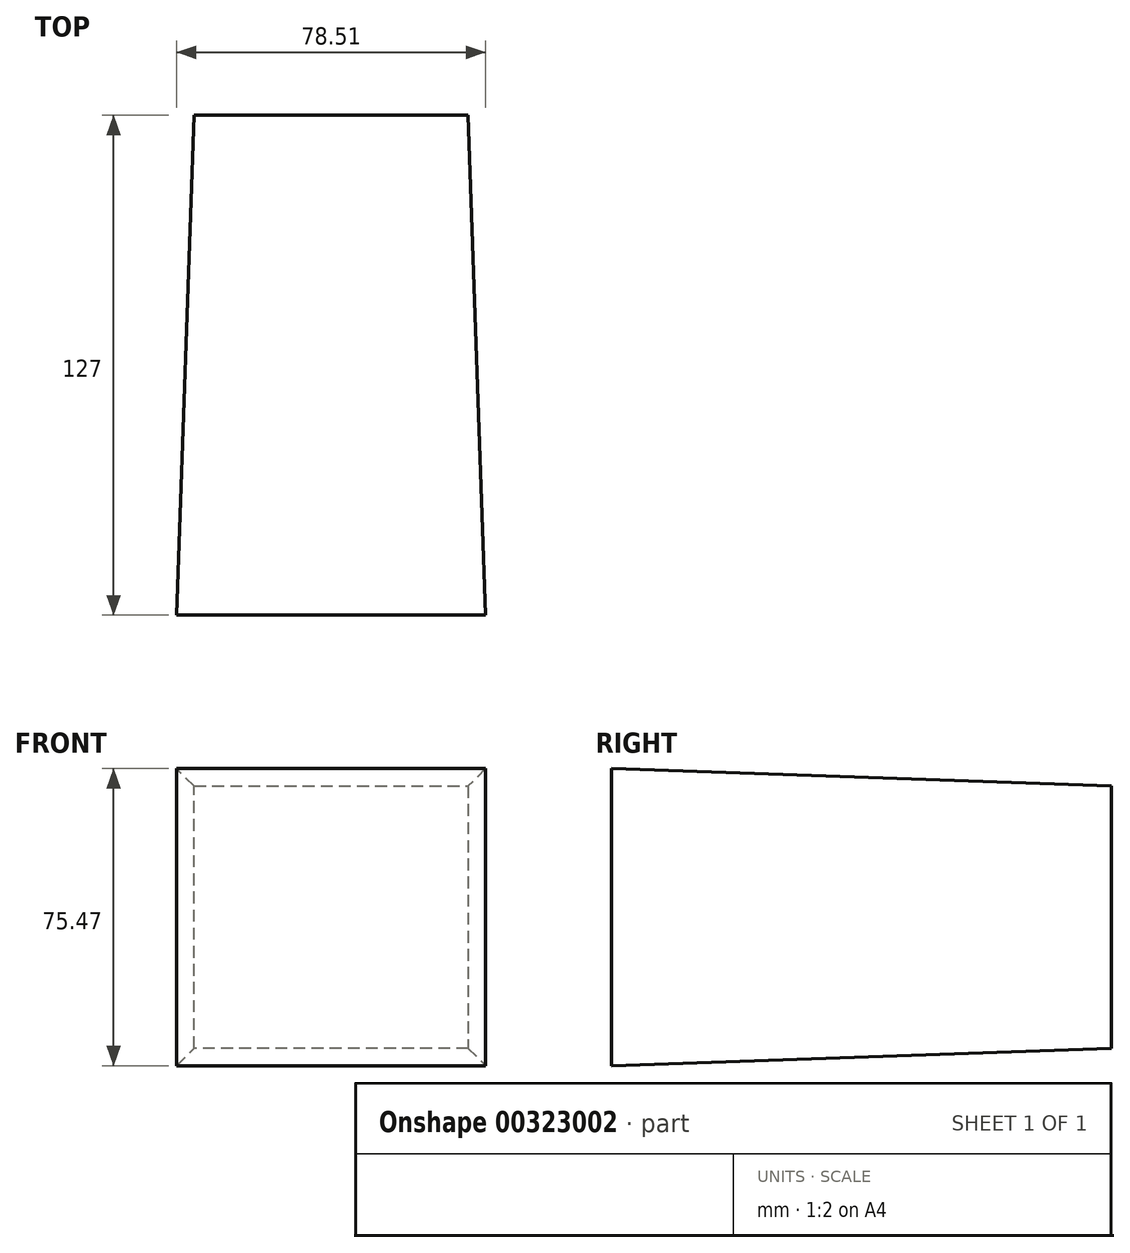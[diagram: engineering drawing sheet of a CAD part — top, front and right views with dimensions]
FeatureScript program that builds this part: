
annotation { "Feature Type Name" : "Feature", "Feature Type Description" : "" }
export const myFeature = defineFeature(function(context is Context, id is Id, definition is map)
    precondition{}
    {
        {
            var Q0;
            Q0=qCreatedBy(makeId("Front.planeOp"),FACE);
            var sketch = newSketch(context, id + "F0", { "sketchPlane" : qUnion([Q0])});
            skLineSegment(sketch, "E0.bottom", {"start": v(-42.19, 30.86) * mm, "end": v(27.46, 30.86) * mm});
            skLineSegment(sketch, "E0.top", {"start": v(-42.19, -35.75) * mm, "end": v(27.46, -35.75) * mm});
            skLineSegment(sketch, "E0.left", {"start": v(-42.19, 30.86) * mm, "end": v(-42.19, -35.75) * mm});
            skLineSegment(sketch, "E0.right", {"start": v(27.46, 30.86) * mm, "end": v(27.46, -35.75) * mm});
            skSolve(sketch);
        }
        {
            var Q0;
            Q0 = qSketchRegion(id + "F0", true);
            extrude(context, id + "F1", {"entities" : qUnion([Q0]), "depth" : 127 * mm, "hasDraft" : true, "draftAngle" : 2 * degree});
        }
    });
